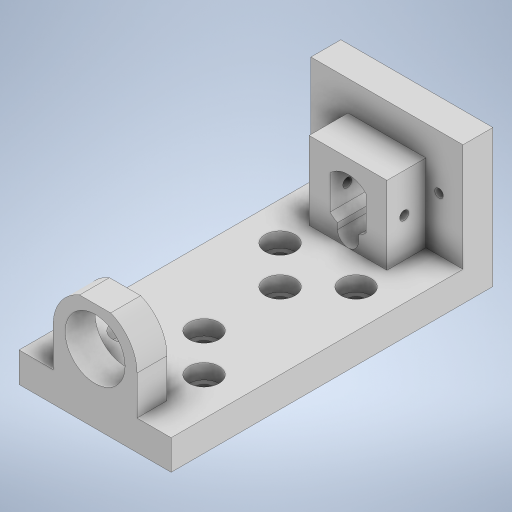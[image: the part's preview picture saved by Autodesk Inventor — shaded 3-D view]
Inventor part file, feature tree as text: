
AUTODESK INVENTOR PART (.ipt)
format: ipt  version: 2024 (Build 280153000, 153)  size: 504,320 bytes
history: native  units: mm
features: projected_geometry x14, extrude x11, sketch x3, plane x1, mirror x1
ambient origin geometry x8: Origin, YZ Plane, XZ Plane, XY Plane, X Axis, Y Axis, Z Axis, Center Point
bodies: Solid1 (feature_tree)
feature tree (30):
  extrude  "Extrusion1"  Depth=50.8mm
  extrude  "Extrusion2"  Depth=5.0mm
  extrude  "Extrusion3"  Depth=10.0mm
  extrude  "Extrusion5"  Depth=10.0mm TaperAngle=0.0deg
  extrude  "Extrusion9"  Depth=10.0mm
  extrude  "Extrusion7"  Depth=87.5mm TaperAngle=0.0deg
  extrude  "Extrusion10"  Depth=20.0mm
  extrude  "Extrusion11"  Depth=10.0mm
  extrude  "Extrusion12"  Depth=5.0mm
  extrude  "Extrusion14"  Depth=5.0mm
  plane  "Work Plane1"
  mirror  "Mirror1"
  extrude  "Extrusion15"  Depth=3.5mm
  sketch  "Sketch1"  dims[d0=25.4mm d1=50.8mm]
  projected_geometry  "Projected Loop1"
  projected_geometry  "Projected Loop2"
  projected_geometry  "Projected Loop4"
  projected_geometry  "Projected Loop5"
  projected_geometry  "Projected Loop7"
  projected_geometry  "Projected Loop9"
  projected_geometry  "Projected Loop10"
  projected_geometry  "Projected Loop11"
  projected_geometry  "Projected Loop12"
  sketch  "Sketch14"  dims[d2=5.0mm d3=5.0mm]
  projected_geometry  "Projected Loop14"
  projected_geometry  "Projected Loop15"
  projected_geometry  "Projected Loop16"
  sketch  "Sketch15"  dims[d4=26.0mm d5=10.0mm d6=10.0mm d7=0.0mm d8=10.0mm d9=87.5mm d10=0.0mm d11=20.0mm d12=38.4mm d13=10.0mm d14=5.0mm d15=5.0mm d16=16.0mm d17=16.0mm d18=5.0mm d19=5.0mm d20=13.0mm d21=0.0mm d24=26.0mm d26=26.0mm d29=2.84mm d30=2.84mm d31=8.0mm d32=8.0mm d33=8.0mm d34=8.0mm d35=26.0mm d36=0.0mm d41=18.0mm d42=26.0mm d43=16.5mm d45=13.0mm d46=12.0mm d47=14.0mm d48=0.0mm d55=10.0mm d56=10.0mm d57=5.0mm d58=0.0mm d59=26.0mm d61=0.0mm d62=180.0deg d63=3.0mm d64=8.25mm d65=11.324752mm d66=5.662376mm d67=0.0mm d68=0.0mm d69=0.0mm d70=26.0mm d71=6.35mm d72=6.35mm d73=13.0mm d75=12.7mm d76=12.7mm d77=10.3mm d78=13.0mm d80=40.0mm d82=25.4mm d83=40.0mm d85=25.4mm d88=12.7mm d89=10.0mm d90=0.0mm d91=10.0mm d92=10.0mm d93=10.0mm d94=5.0mm d95=0.0mm d99=13.0mm d100=20.0mm d101=28.0mm d102=6.0mm d103=6.0mm d104=10.0mm d105=0.0mm d106=18.0mm d107=0.0mm d108=58.4mm d109=7.0mm d110=0.0mm d111=8.25mm d113=3.5mm d114=0.0mm d115=0.0mm d116=5.5mm d117=0.0mm]
  projected_geometry  "Projected Loop17"
  projected_geometry  "Projected Loop18"
